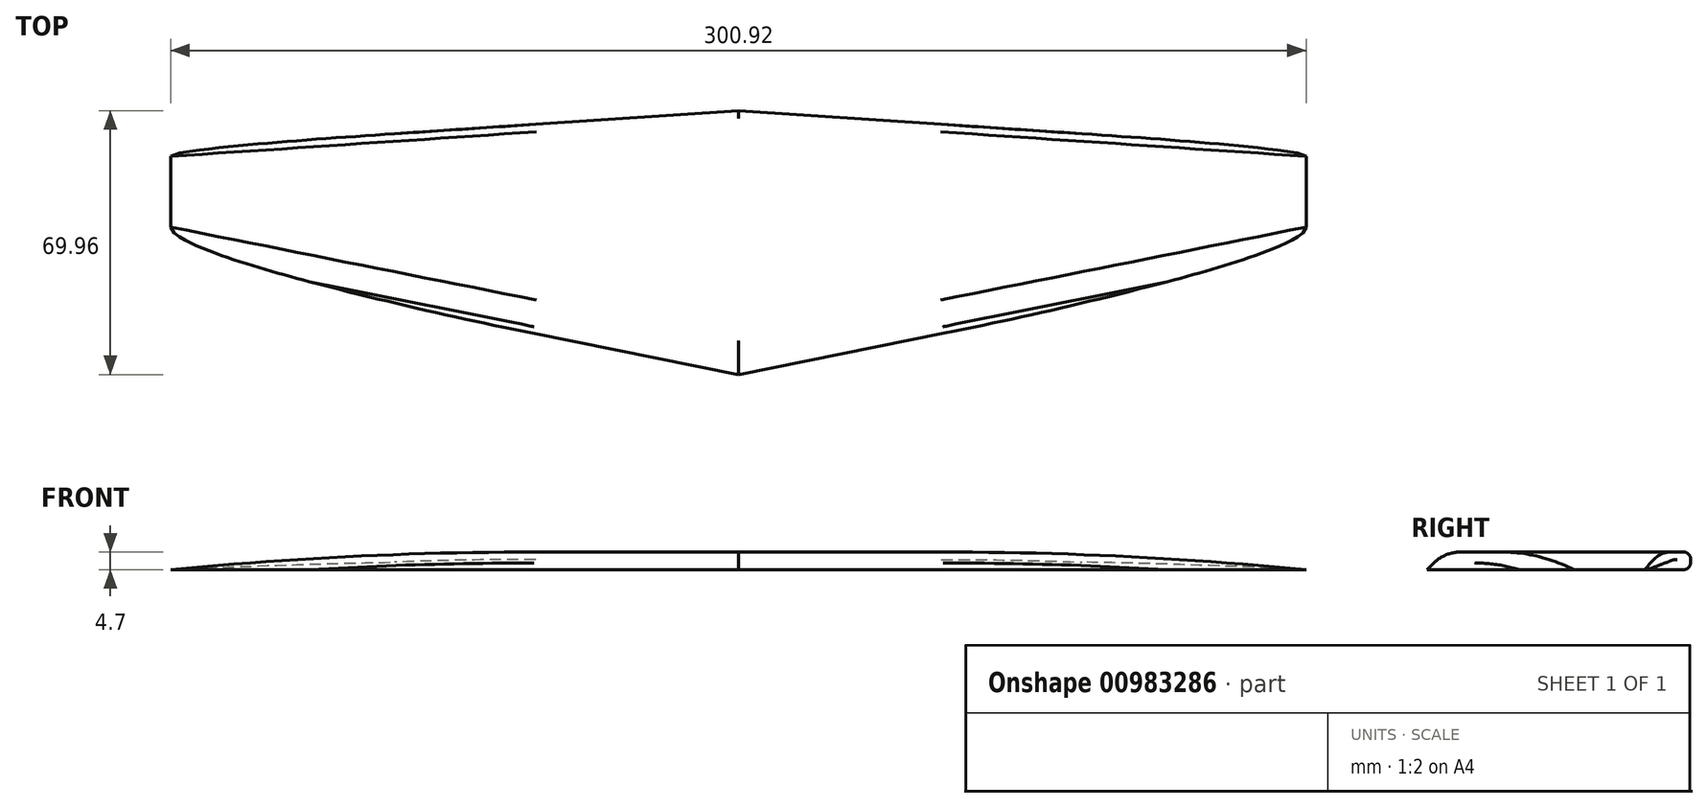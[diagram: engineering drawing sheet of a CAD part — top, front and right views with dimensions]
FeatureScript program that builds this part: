
annotation { "Feature Type Name" : "Feature", "Feature Type Description" : "" }
export const myFeature = defineFeature(function(context is Context, id is Id, definition is map)
    precondition{}
    {
        {
            var Q0;
            Q0=qCreatedBy(makeId("Top.planeOp"),FACE);
            var sketch = newSketch(context, id + "F0", { "sketchPlane" : qUnion([Q0])});
            skLineSegment(sketch, "E0", {"start": v(0, -45.26) * mm, "end": v(0, 25) * mm});
            skLineSegment(sketch, "E1", {"start": v(0, 25) * mm, "end": v(151.1, 14.89) * mm});
            skLineSegment(sketch, "E2", {"start": v(151.1, 14.89) * mm, "end": v(151.1, -14.89) * mm});
            skLineSegment(sketch, "E3", {"start": v(151.1, -14.89) * mm, "end": v(0, -45.26) * mm});
            skSolve(sketch);
        }
        {
            var Q0;
            Q0 = qSketchRegion(id + "F0", true);
            extrude(context, id + "F1", {"entities" : qUnion([Q0]), "depth" : 4.7 * mm, "offsetDistance" : 25 * mm});
        }
        {
            var Q0;
            Q0=makeQuery(id+"F1.opExtrude","CAP_EDGE",EDGE,{"disambiguationData":[OSD([sQuery(id+"F0.wireOp",EDGE,"E2")])],"isStart":false});
            chamfer(context, id + "F2", {"entities" : qUnion([Q0]), "chamferType" : ChamferType.OFFSET_ANGLE, "width" : 5 * mm, "oppositeDirection" : false, "angle" : 65 * degree, "tangentPropagation" : true});
        }
        {
            var Q0;
            {var subQ0=sQuery(id+"F0.wireOp",EDGE,"E2");Q0=makeQuery(id+"F2.opChamfer","BLEND_EDGE",EDGE,{"blendedFrom":[makeQuery(id+"F1.opExtrude","CAP_EDGE",EDGE,{"disambiguationData":[OSD([subQ0])],"isStart":false}),makeQuery(id+"F1.opExtrude","CAP_FACE",FACE,{"disambiguationData":[OSD([sQuery(id+"F0.wireOp",EDGE,"E0"),sQuery(id+"F0.wireOp",EDGE,"E1"),subQ0,sQuery(id+"F0.wireOp",EDGE,"E3")])],"isStart":false})],"blendedInto":[makeQuery(id+"F1.opExtrude","CAP_FACE",FACE,{"disambiguationData":[OSD([sQuery(id+"F0.wireOp",EDGE,"E0"),sQuery(id+"F0.wireOp",EDGE,"E1"),subQ0,sQuery(id+"F0.wireOp",EDGE,"E3")])],"isStart":false})]});}
            fillet(context, id + "F3", {"entities" : qUnion([Q0]), "radius" : 1000 * mm, "tangentPropagation" : true, "allowEdgeOverflow" : false});
        }
        {
            var Q0;
            {var subQ0=sQuery(id+"F0.wireOp",EDGE,"E1");var subQ1=sQuery(id+"F0.wireOp",EDGE,"E2");Q0=makeQuery(id+"F3.opFillet","BLEND_EDGE",EDGE,{"blendedFrom":[makeQuery(id+"F2.opChamfer","BLEND_EDGE",EDGE,{"blendedFrom":[makeQuery(id+"F1.opExtrude","CAP_EDGE",EDGE,{"disambiguationData":[OSD([subQ1])],"isStart":false}),makeQuery(id+"F1.opExtrude","CAP_FACE",FACE,{"disambiguationData":[OSD([sQuery(id+"F0.wireOp",EDGE,"E0"),subQ0,subQ1,sQuery(id+"F0.wireOp",EDGE,"E3")])],"isStart":false})],"blendedInto":[makeQuery(id+"F1.opExtrude","CAP_FACE",FACE,{"disambiguationData":[OSD([sQuery(id+"F0.wireOp",EDGE,"E0"),subQ0,subQ1,sQuery(id+"F0.wireOp",EDGE,"E3")])],"isStart":false})]}),makeQuery(id+"F1.opExtrude","SWEPT_FACE",FACE,{"disambiguationData":[OSD([subQ0])]})],"blendedInto":[makeQuery(id+"F1.opExtrude","SWEPT_FACE",FACE,{"disambiguationData":[OSD([subQ0])]})]});}
            var Q1;
            Q1=makeQuery(id+"F1.opExtrude","CAP_EDGE",EDGE,{"disambiguationData":[OSD([sQuery(id+"F0.wireOp",EDGE,"E1")])],"isStart":false});
            var Q2;
            Q2=makeQuery(id+"F1.opExtrude","CAP_EDGE",EDGE,{"disambiguationData":[OSD([sQuery(id+"F0.wireOp",EDGE,"E1")])],"isStart":true});
            fillet(context, id + "F4", {"entities" : qUnion([Q0, Q1, Q2]), "radius" : 2 * mm, "tangentPropagation" : true, "allowEdgeOverflow" : false});
        }
        {
            var Q0;
            {var subQ0=sQuery(id+"F0.wireOp",EDGE,"E3");var subQ1=sQuery(id+"F0.wireOp",EDGE,"E2");Q0=makeQuery(id+"F3.opFillet","BLEND_EDGE",EDGE,{"blendedFrom":[makeQuery(id+"F2.opChamfer","BLEND_EDGE",EDGE,{"blendedFrom":[makeQuery(id+"F1.opExtrude","CAP_EDGE",EDGE,{"disambiguationData":[OSD([subQ1])],"isStart":false}),makeQuery(id+"F1.opExtrude","CAP_FACE",FACE,{"disambiguationData":[OSD([sQuery(id+"F0.wireOp",EDGE,"E0"),sQuery(id+"F0.wireOp",EDGE,"E1"),subQ1,subQ0])],"isStart":false})],"blendedInto":[makeQuery(id+"F1.opExtrude","CAP_FACE",FACE,{"disambiguationData":[OSD([sQuery(id+"F0.wireOp",EDGE,"E0"),sQuery(id+"F0.wireOp",EDGE,"E1"),subQ1,subQ0])],"isStart":false})]}),makeQuery(id+"F1.opExtrude","SWEPT_FACE",FACE,{"disambiguationData":[OSD([subQ0])]})],"blendedInto":[makeQuery(id+"F1.opExtrude","SWEPT_FACE",FACE,{"disambiguationData":[OSD([subQ0])]})]});}
            var Q1;
            Q1=makeQuery(id+"F1.opExtrude","CAP_EDGE",EDGE,{"disambiguationData":[OSD([sQuery(id+"F0.wireOp",EDGE,"E3")])],"isStart":false});
            chamfer(context, id + "F5", {"entities" : qUnion([Q0, Q1]), "width" : 5 * mm, "tangentPropagation" : true});
        }
        {
            var Q0;
            {var subQ0=sQuery(id+"F0.wireOp",EDGE,"E3");Q0=makeQuery(id+"F5.opChamfer","BLEND_EDGE",EDGE,{"blendedFrom":[makeQuery(id+"F1.opExtrude","CAP_EDGE",EDGE,{"disambiguationData":[OSD([subQ0])],"isStart":false}),makeQuery(id+"F1.opExtrude","CAP_FACE",FACE,{"disambiguationData":[OSD([sQuery(id+"F0.wireOp",EDGE,"E0"),sQuery(id+"F0.wireOp",EDGE,"E1"),sQuery(id+"F0.wireOp",EDGE,"E2"),subQ0])],"isStart":false})],"blendedInto":[makeQuery(id+"F1.opExtrude","CAP_FACE",FACE,{"disambiguationData":[OSD([sQuery(id+"F0.wireOp",EDGE,"E0"),sQuery(id+"F0.wireOp",EDGE,"E1"),sQuery(id+"F0.wireOp",EDGE,"E2"),subQ0])],"isStart":false})]});}
            var Q1;
            {var subQ0=sQuery(id+"F0.wireOp",EDGE,"E3");var subQ1=sQuery(id+"F0.wireOp",EDGE,"E2");var subQ2=sQuery(id+"F0.wireOp",EDGE,"E1");var subQ3=sQuery(id+"F0.wireOp",EDGE,"E0");Q1=makeQuery(id+"F5.opChamfer","BLEND_EDGE",EDGE,{"blendedFrom":[makeQuery(id+"F3.opFillet","BLEND_EDGE",EDGE,{"blendedFrom":[makeQuery(id+"F2.opChamfer","BLEND_EDGE",EDGE,{"blendedFrom":[makeQuery(id+"F1.opExtrude","CAP_EDGE",EDGE,{"disambiguationData":[OSD([subQ1])],"isStart":false}),makeQuery(id+"F1.opExtrude","CAP_FACE",FACE,{"disambiguationData":[OSD([subQ3,subQ2,subQ1,subQ0])],"isStart":false})],"blendedInto":[makeQuery(id+"F1.opExtrude","CAP_FACE",FACE,{"disambiguationData":[OSD([subQ3,subQ2,subQ1,subQ0])],"isStart":false})]}),makeQuery(id+"F1.opExtrude","SWEPT_FACE",FACE,{"disambiguationData":[OSD([subQ0])]})],"blendedInto":[makeQuery(id+"F1.opExtrude","SWEPT_FACE",FACE,{"disambiguationData":[OSD([subQ0])]})]}),makeQuery(id+"F3.opFillet","BLEND_FACE",FACE,{"disambiguationData":[OSD([subQ3,subQ2,subQ1,subQ0])]})],"blendedInto":[makeQuery(id+"F3.opFillet","BLEND_FACE",FACE,{"disambiguationData":[OSD([subQ3,subQ2,subQ1,subQ0])]})]});}
            fillet(context, id + "F6", {"entities" : qUnion([Q0, Q1]), "radius" : 10 * mm, "tangentPropagation" : true, "allowEdgeOverflow" : false});
        }
        {
            var Q0;
            Q0=makeQuery(id+"F1.opExtrude","SWEPT_BODY",BODY,{"disambiguationData":[OSD([sQuery(id+"F0.wireOp",EDGE,"E0"),sQuery(id+"F0.wireOp",EDGE,"E1"),sQuery(id+"F0.wireOp",EDGE,"E2"),sQuery(id+"F0.wireOp",EDGE,"E3")])]});
            var Q1;
            Q1=qCreatedBy(makeId("Right.planeOp"),FACE);
            mirror(context, id + "F7", {"operationType" : NewBodyOperationType.ADD, "entities" : qUnion([Q0]), "mirrorPlane" : qUnion([Q1])});
        }
    });
